# Revit family: НЕВАТОМ_Козырек защитный ВР, версия 1
name_source: partatom
category: Оборудование
revit_build: Autodesk Revit 2017 (Build: 20170118_1100(x64)
units: mm (PartAtom-declared; Revit-internal decimal feet)

## family parameters
Всегда вертикально = Нет
На основе рабочей плоскости = Нет
Общий = Нет
При загрузке вырезать с полостями = Нет
Размер круглого соединителя = Использовать диаметр
Тип детали = Нормальный
Точка расчета площади = Нет

## types (14) — shared parameters
ADSK_Единица измерения = шт.
ADSK_Завод-изготовитель = НЕВАТОМ
ADSK_Количество = 1
ADSK_Материал наименование = сталь оцинкованная
Nevatom_URL = https://t.me
толщина козырька = 4 мм

## per-type parameters (varying)
| type | A | ADSK_Марка | H | H1 | L | С | вверх вырез |
| Козырек защитный  ВР №2,0 | 140 мм | ВР №2,0 | 270 мм | 200 мм | 100 мм | 310 мм | 280 мм |
| Козырек защитный  ВР №2,5 | 175 мм | ВР №2,5 | 270 мм | 200 мм | 100 мм | 360 мм | 280 мм |
| Козырек защитный  ВР №3,15 | 221 мм | ВР №3,15 | 400 мм | 250 мм | 100 мм | 490 мм | 410 мм |
| Козырек защитный  ВР №4,0 | 280 мм | ВР №4,0 | 400 мм | 250 мм | 100 мм | 540 мм | 410 мм |
| Козырек защитный  ВР №4,5 | 315 мм | ВР №4,5 | 400 мм | 250 мм | 100 мм | 540 мм | 410 мм |
| Козырек защитный  ВР №5,0 | 350 мм | ВР №5,0 | 400 мм | 250 мм | 100 мм | 590 мм | 410 мм |
| Козырек защитный  ВР №5,6 | 392 мм | ВР №5,6 | 400 мм | 250 мм | 100 мм | 640 мм | 410 мм |
| Козырек защитный  ВР №6,3 | 441 мм | ВР №6,3 | 400 мм | 250 мм | 100 мм | 655 мм | 410 мм |
| Козырек защитный  ВР №7,1 | 497 мм | ВР №7,1 | 400 мм | 250 мм | 100 мм | 690 мм | 410 мм |
| Козырек защитный  ВР №8,0 | 560 мм | ВР №8,0 | 480 мм | 280 мм | 30 мм | 950 мм | 490 мм |
| Козырек защитный  ВР №9,0 | 630 мм | ВР №9,0 | 480 мм | 280 мм | 30 мм | 1050 мм | 490 мм |
| Козырек защитный  ВР №10,0 | 700 мм | ВР №10,0 | 480 мм | 280 мм | 30 мм | 1100 мм | 490 мм |
| Козырек защитный  ВР №11,2 | 784 мм | ВР №11,2 | 580 мм | 330 мм | 30 мм | 1280 мм | 590 мм |
| Козырек защитный  ВР №12,5 | 875 мм | ВР №12,5 | 580 мм | 330 мм | 30 мм | 1330 мм | 590 мм |

note: column(s) folded — value = type name in every type: ADSK_Наименование
